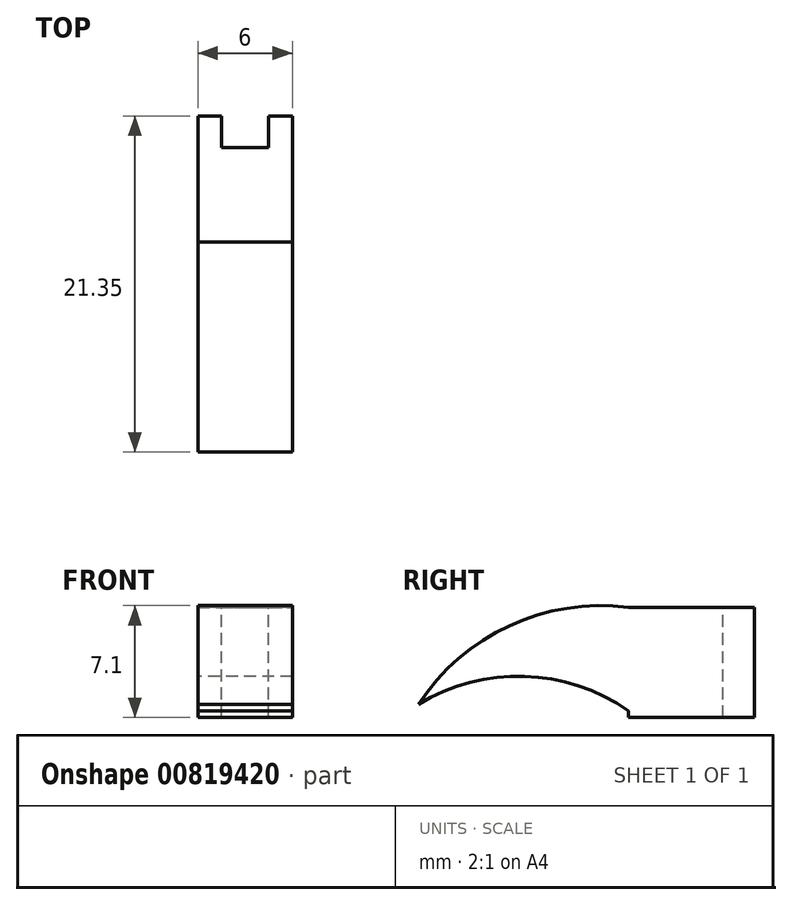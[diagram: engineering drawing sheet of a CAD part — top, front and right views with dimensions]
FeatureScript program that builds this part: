
annotation { "Feature Type Name" : "Feature", "Feature Type Description" : "" }
export const myFeature = defineFeature(function(context is Context, id is Id, definition is map)
    precondition{}
    {
        {
            var Q0;
            Q0=qCreatedBy(makeId("Front.planeOp"),FACE);
            var sketch = newSketch(context, id + "F0", { "sketchPlane" : qUnion([Q0])});
            skLineSegment(sketch, "E0.bottom", {"start": v(-3, 9.98) * mm, "end": v(3, 9.98) * mm});
            skLineSegment(sketch, "E0.top", {"start": v(-3, 16.98) * mm, "end": v(3, 16.98) * mm});
            skLineSegment(sketch, "E0.left", {"start": v(-3, 9.98) * mm, "end": v(-3, 16.98) * mm});
            skLineSegment(sketch, "E0.right", {"start": v(3, 9.98) * mm, "end": v(3, 16.98) * mm});
            skPoint(sketch, "E0.middle", {"position": v(0, 13.48) * mm});
            skSolve(sketch);
        }
        {
            var Q0;
            Q0 = qSketchRegion(id + "F0", true);
            extrude(context, id + "F1", {"entities" : qUnion([Q0]), "depth" : 8 * mm, "offsetDistance" : 25 * mm});
        }
        {
            var Q0;
            Q0=qCreatedBy(makeId("Front.planeOp"),FACE);
            var sketch = newSketch(context, id + "F2", { "sketchPlane" : qUnion([Q0])});
            skLineSegment(sketch, "E1.bottom", {"start": v(-1.5, 9.72) * mm, "end": v(1.5, 9.72) * mm});
            skLineSegment(sketch, "E1.top", {"start": v(-1.5, 17.22) * mm, "end": v(1.5, 17.22) * mm});
            skLineSegment(sketch, "E1.left", {"start": v(-1.5, 9.72) * mm, "end": v(-1.5, 17.22) * mm});
            skLineSegment(sketch, "E1.right", {"start": v(1.5, 9.72) * mm, "end": v(1.5, 17.22) * mm});
            skPoint(sketch, "E1.middle", {"position": v(0, 13.47) * mm});
            skSolve(sketch);
        }
        {
            var Q0;
            Q0 = qSketchRegion(id + "F2", true);
            extrude(context, id + "F3", {"entities" : qUnion([Q0]), "operationType" : NewBodyOperationType.REMOVE, "depth" : 2 * mm, "offsetDistance" : 25 * mm});
        }
        {
            var Q0;
            Q0=qCreatedBy(makeId("Right.planeOp"),FACE);
            var sketch = newSketch(context, id + "F4", { "sketchPlane" : qUnion([Q0])});
            skArc(sketch, "E2", {"start": v(-6.65, 16.73) * mm, "mid": v(-14.93, 16.08) * mm, "end": v(-21.35, 10.8) * mm});
            skArc(sketch, "E3", {"start": v(-7.87, 10.3) * mm, "mid": v(-14.53, 12.59) * mm, "end": v(-21.35, 10.8) * mm});
            skLineSegment(sketch, "E4", {"start": v(-7.87, 10.3) * mm, "end": v(-6.65, 16.73) * mm});
            skSolve(sketch);
        }
        {
            var Q0;
            Q0=makeQuery(id+"F4.imprint","IMPRINT",FACE,{"disambiguationData":[TD([[makeQuery(id+"F4.imprint","IMPRINT",EDGE,{"derivedFrom":sQuery(id+"F4.wireOp",EDGE,"E2")}),1.0]])]});
            extrude(context, id + "F5", {"entities" : qUnion([Q0]), "operationType" : NewBodyOperationType.ADD, "endBound" : BoundingType.SYMMETRIC, "depth" : 6 * mm, "offsetDistance" : 25 * mm});
        }
    });
